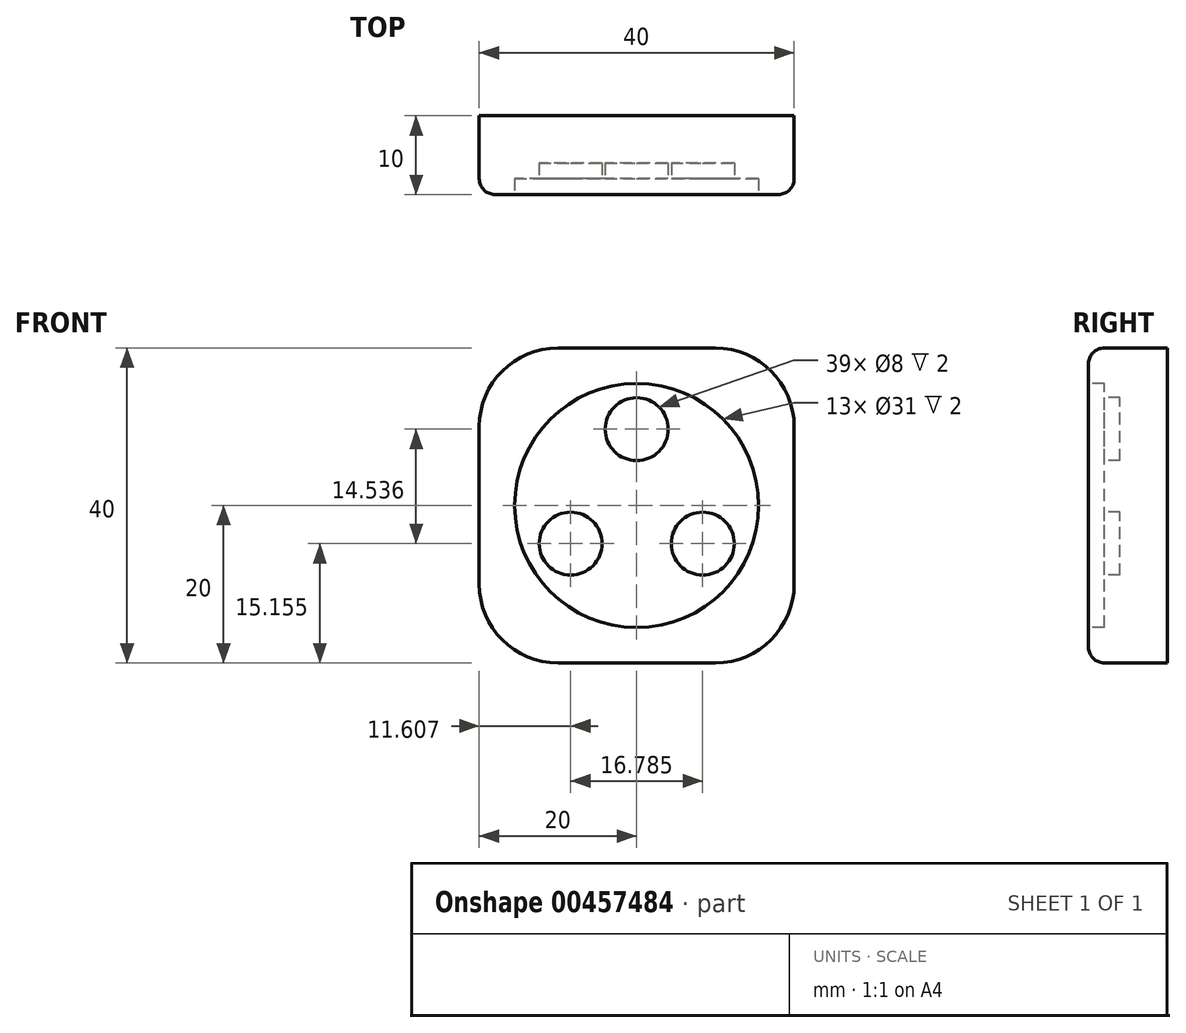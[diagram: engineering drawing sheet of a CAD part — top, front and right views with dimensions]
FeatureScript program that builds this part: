
annotation { "Feature Type Name" : "Feature", "Feature Type Description" : "" }
export const myFeature = defineFeature(function(context is Context, id is Id, definition is map)
    precondition{}
    {
        {
            var Q0;
            Q0=qCreatedBy(makeId("Front.planeOp"),FACE);
            var sketch = newSketch(context, id + "F0", { "sketchPlane" : qUnion([Q0])});
            skLineSegment(sketch, "E0.bottom", {"start": v(-20, 20) * mm, "end": v(20, 20) * mm});
            skLineSegment(sketch, "E0.top", {"start": v(-20, -20) * mm, "end": v(20, -20) * mm});
            skLineSegment(sketch, "E0.left", {"start": v(-20, 20) * mm, "end": v(-20, -20) * mm});
            skLineSegment(sketch, "E0.right", {"start": v(20, 20) * mm, "end": v(20, -20) * mm});
            skSolve(sketch);
        }
        {
            var Q0;
            Q0 = qSketchRegion(id + "F0", true);
            extrude(context, id + "F1", {"entities" : qUnion([Q0]), "depth" : 10 * mm});
        }
        {
            var Q0;
            Q0=makeQuery(id+"F1.opExtrude","CAP_FACE",FACE,{"disambiguationData":[OSD([sQuery(id+"F0.wireOp",EDGE,"E0.bottom"),sQuery(id+"F0.wireOp",EDGE,"E0.top"),sQuery(id+"F0.wireOp",EDGE,"E0.left"),sQuery(id+"F0.wireOp",EDGE,"E0.right")])],"isStart":false});
            var sketch = newSketch(context, id + "F2", { "sketchPlane" : qUnion([Q0])});
            skCircle(sketch, "E1", {"center": v(0, 0) * mm, "radius": 15.5 * mm});
            skSolve(sketch);
        }
        {
            var Q0;
            Q0 = qSketchRegion(id + "F2", true);
            extrude(context, id + "F3", {"entities" : qUnion([Q0]), "operationType" : NewBodyOperationType.REMOVE, "oppositeDirection" : true, "depth" : 2 * mm});
        }
        {
            var Q0;
            Q0=makeQuery(id+"F3.boolean.opBoolean","COPY",FACE,{"derivedFrom":makeQuery(id+"F3.opExtrude","CAP_FACE",FACE,{"disambiguationData":[OSD([sQuery(id+"F2.wireOp",EDGE,"E1")])],"isStart":false})});
            var sketch = newSketch(context, id + "F4", { "sketchPlane" : qUnion([Q0])});
            skCircle(sketch, "E2", {"center": v(0, 9.7) * mm, "radius": 4 * mm});
            skLineSegment(sketch, "E3", {"start": v(0, 0) * mm, "end": v(0, 26.53) * mm, "construction": true});
            skCircle(sketch, "E4.1.0", {"center": v(-8.4, -4.85) * mm, "radius": 4 * mm});
            skCircle(sketch, "E4.2.0", {"center": v(8.4, -4.85) * mm, "radius": 4 * mm});
            skPoint(sketch, "E4.center", {"position": v(0, 0) * mm});
            skSolve(sketch);
        }
        {
            var Q0;
            Q0 = qSketchRegion(id + "F4", true);
            extrude(context, id + "F5", {"entities" : qUnion([Q0]), "operationType" : NewBodyOperationType.REMOVE, "oppositeDirection" : true, "depth" : 2 * mm});
        }
        {
            var Q0;
            Q0=makeQuery(id+"F1.opExtrude","CAP_EDGE",EDGE,{"disambiguationData":[OSD([sQuery(id+"F0.wireOp",EDGE,"E0.bottom")])],"isStart":false});
            var Q1;
            Q1=makeQuery(id+"F1.opExtrude","CAP_EDGE",EDGE,{"disambiguationData":[OSD([sQuery(id+"F0.wireOp",EDGE,"E0.left")])],"isStart":false});
            var Q2;
            Q2=makeQuery(id+"F1.opExtrude","CAP_EDGE",EDGE,{"disambiguationData":[OSD([sQuery(id+"F0.wireOp",EDGE,"E0.right")])],"isStart":false});
            var Q3;
            Q3=makeQuery(id+"F1.opExtrude","CAP_EDGE",EDGE,{"disambiguationData":[OSD([sQuery(id+"F0.wireOp",EDGE,"E0.top")])],"isStart":false});
            fillet(context, id + "F6", {"entities" : qUnion([Q0, Q1, Q2, Q3]), "radius" : 2 * mm, "tangentPropagation" : true, "allowEdgeOverflow" : false});
        }
        {
            var Q0;
            Q0=makeQuery(id+"F1.opExtrude","SWEPT_EDGE",EDGE,{"disambiguationData":[OSD([sQuery(id+"F0.wireOp",EDGE,"E0.bottom"),sQuery(id+"F0.wireOp",EDGE,"E0.right")])]});
            var Q1;
            Q1=makeQuery(id+"F1.opExtrude","SWEPT_EDGE",EDGE,{"disambiguationData":[OSD([sQuery(id+"F0.wireOp",EDGE,"E0.bottom"),sQuery(id+"F0.wireOp",EDGE,"E0.left")])]});
            var Q2;
            Q2=makeQuery(id+"F1.opExtrude","SWEPT_EDGE",EDGE,{"disambiguationData":[OSD([sQuery(id+"F0.wireOp",EDGE,"E0.top"),sQuery(id+"F0.wireOp",EDGE,"E0.right")])]});
            var Q3;
            Q3=makeQuery(id+"F1.opExtrude","SWEPT_EDGE",EDGE,{"disambiguationData":[OSD([sQuery(id+"F0.wireOp",EDGE,"E0.top"),sQuery(id+"F0.wireOp",EDGE,"E0.left")])]});
            fillet(context, id + "F7", {"entities" : qUnion([Q0, Q1, Q2, Q3]), "radius" : 10 * mm, "tangentPropagation" : true, "allowEdgeOverflow" : false});
        }
    });
